# Revit family: P2004-09 1-100W MED BATH BRACKET
name_source: partatom
category: Lighting Fixtures
revit_build: Autodesk Revit Architecture 2012 (Build: 20110309_2315(x64)
units: mm (PartAtom-declared; Revit-internal decimal feet)

## types (1)
- P2004-09 1-100W MED BATH BRACKET
    Back Plate = Brushed Nickel
    Color Filter = 16777215
    Default Elevation = 48"
    Description = One light bath fixture with fluted glass shades
    Dimming Lamp Color Temperature Shift = <None>
    Glass = White Etched Glass
    Lamp = One
    Lamp Type = Medium Base
    Light Source Symbol Size = 3"
    Manufacturer = Progresslighting
    Manufacturer Fax Number = (864)-678-1065
    Model = P2004-09
    Mounting = Wall Mount
    Product Documentation Link = https://progresslighting.com
    Product Page URL = https://progresslighting.com
    URL = https://progresslighting.com
    Wattage Comments = 100

## geometry (parser evidence)
native form markers: Sweep x3
no freeform markers — native parametric forms only
